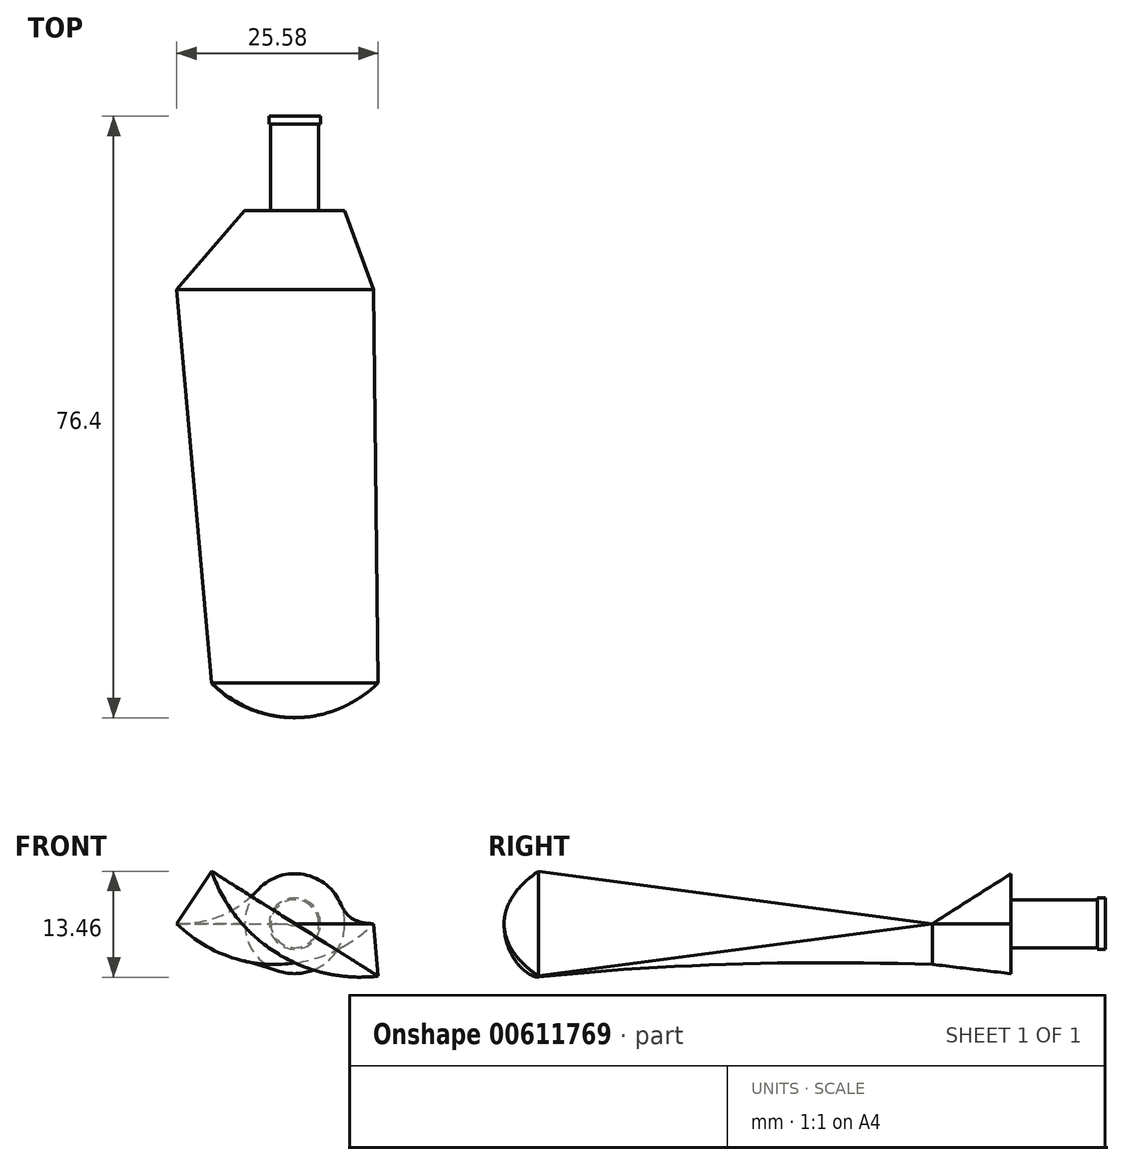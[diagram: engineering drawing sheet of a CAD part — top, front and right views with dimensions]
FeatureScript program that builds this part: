
annotation { "Feature Type Name" : "Feature", "Feature Type Description" : "" }
export const myFeature = defineFeature(function(context is Context, id is Id, definition is map)
    precondition{}
    {
        {
            var Q0;
            Q0=qCreatedBy(makeId("Front.planeOp"),FACE);
            var sketch = newSketch(context, id + "F0", { "sketchPlane" : qUnion([Q0])});
            skCircle(sketch, "E0", {"center": v(0, 0) * mm, "radius": 6.35 * mm});
            skSolve(sketch);
        }
        {
            var Q0;
            Q0=qCreatedBy(makeId("Front.planeOp"),FACE);
            cPlane(context, id + "F1", {"entities" : qUnion([Q0]), "cplaneType" : CPlaneType.OFFSET, "offset" : 10 * mm, "width" : 152.4 * mm, "height" : 152.4 * mm});
        }
        {
            var Q0;
            Q0=qCreatedBy(id+"F1.planeOp",FACE);
            cPlane(context, id + "F2", {"entities" : qUnion([Q0]), "cplaneType" : CPlaneType.OFFSET, "offset" : 50 * mm, "width" : 152.4 * mm, "height" : 152.4 * mm});
        }
        {
            var Q0;
            Q0=qCreatedBy(id+"F1.planeOp",FACE);
            var sketch = newSketch(context, id + "F3", { "sketchPlane" : qUnion([Q0])});
            skLineSegment(sketch, "E1", {"start": v(0, 0) * mm, "end": v(10, 0) * mm, "construction": true});
            skLineSegment(sketch, "E2", {"start": v(0, 0) * mm, "end": v(-15, 0) * mm, "construction": true});
            skLineSegment(sketch, "E3", {"start": v(0, 0) * mm, "end": v(0, 12.7) * mm, "construction": true});
            skLineSegment(sketch, "E4", {"start": v(0, 0) * mm, "end": v(0, -5) * mm, "construction": true});
            skArc(sketch, "E5", {"start": v(-15, 0) * mm, "mid": v(-2.5, -5.18) * mm, "end": v(10, 0) * mm});
            skLineSegment(sketch, "E6", {"start": v(-15, 0) * mm, "end": v(10, 0) * mm});
            skSolve(sketch);
        }
        {
            var Q0;
            Q0=qCreatedBy(id+"F2.planeOp",FACE);
            var sketch = newSketch(context, id + "F4", { "sketchPlane" : qUnion([Q0])});
            skLineSegment(sketch, "E7", {"start": v(0, 0) * mm, "end": v(12.7, 0) * mm, "construction": true});
            skLineSegment(sketch, "E8", {"start": v(0, 0) * mm, "end": v(-12.7, 0) * mm, "construction": true});
            skLineSegment(sketch, "E9", {"start": v(-12.7, 0) * mm, "end": v(-12.7, 8) * mm, "construction": true});
            skLineSegment(sketch, "E10", {"start": v(12.7, 0) * mm, "end": v(12.7, -8) * mm, "construction": true});
            skLineSegment(sketch, "E11", {"start": v(-12.7, 8) * mm, "end": v(12.7, -8) * mm, "construction": true});
            skLineSegment(sketch, "E12", {"start": v(0, 0) * mm, "end": v(-10.58, 6.66) * mm, "construction": true});
            skLineSegment(sketch, "E13", {"start": v(0, 0) * mm, "end": v(10.58, -6.66) * mm, "construction": true});
            skLineSegment(sketch, "E14", {"start": v(-10.58, 6.66) * mm, "end": v(10.58, -6.66) * mm});
            skArc(sketch, "E15", {"start": v(-10.58, 6.66) * mm, "mid": v(-2.34, -3.71) * mm, "end": v(10.58, -6.66) * mm});
            skSolve(sketch);
        }
        {
            var Q0;
            Q0=makeQuery(id+"F0.imprint","IMPRINT",FACE,{"disambiguationData":[TD([[makeQuery(id+"F0.imprint","IMPRINT",EDGE,{"derivedFrom":sQuery(id+"F0.wireOp",EDGE,"E0")}),1.0]])]});
            var Q1;
            Q1=makeQuery(id+"F3.imprint","IMPRINT",FACE,{"disambiguationData":[TD([[makeQuery(id+"F3.imprint","IMPRINT",EDGE,{"derivedFrom":sQuery(id+"F3.wireOp",EDGE,"E5")}),1.0]])]});
            loft(context, id + "F5", {"sheetProfilesArray" : [{ "sheetProfileEntities" : qUnion([Q0]) }, { "sheetProfileEntities" : qUnion([Q1]) }]});
        }
        {
            var Q1;
            Q1=makeQuery(id+"F3.imprint","IMPRINT",FACE,{"disambiguationData":[TD([[makeQuery(id+"F3.imprint","IMPRINT",EDGE,{"derivedFrom":sQuery(id+"F3.wireOp",EDGE,"E5")}),1.0]])]});
            var Q2;
            {var subQ0=sQuery(id+"F4.wireOp",EDGE,"E15");Q2=makeQuery(id+"F4.imprint","IMPRINT",FACE,{"disambiguationData":[TD([[makeQuery(id+"F4.imprint","IMPRINT",EDGE,{"derivedFrom":subQ0}),1.0]])]});}
            loft(context, id + "F6", {"operationType" : NewBodyOperationType.ADD, "sheetProfilesArray" : [{ "sheetProfileEntities" : qUnion([Q1]) }, { "sheetProfileEntities" : qUnion([Q2]) }]});
        }
        {
            var Q0;
            Q0=makeQuery(id+"F5.opLoft","CAP_FACE",FACE,{"disambiguationData":[OSD([makeQuery(id+"F0.imprint","IMPRINT",FACE,{"disambiguationData":[TD([[makeQuery(id+"F0.imprint","IMPRINT",EDGE,{"derivedFrom":sQuery(id+"F0.wireOp",EDGE,"E0")}),1.0]])]})])],"isStart":true});
            var sketch = newSketch(context, id + "F7", { "sketchPlane" : qUnion([Q0])});
            skCircle(sketch, "E16", {"center": v(0, 0) * mm, "radius": 3.05 * mm});
            skSolve(sketch);
        }
        {
            var Q0;
            Q0=qSketchRegion(id+"F7",true);
            extrude(context, id + "F8", {"entities" : qUnion([Q0]), "operationType" : NewBodyOperationType.ADD, "depth" : 11 * mm});
        }
        {
            var Q0;
            Q0=makeQuery(id+"F6.opLoft","CAP_FACE",FACE,{"disambiguationData":[OSD([makeQuery(id+"F4.imprint","IMPRINT",FACE,{"disambiguationData":[TD([[makeQuery(id+"F4.imprint","IMPRINT",EDGE,{"derivedFrom":sQuery(id+"F4.wireOp",EDGE,"E14")}),-1.0]])]})])],"isStart":true});
            var sketch = newSketch(context, id + "F9", { "sketchPlane" : qUnion([Q0])});
            skLineSegment(sketch, "E17.0.0", {"start": v(10.58, -6.66) * mm, "end": v(-10.58, 6.66) * mm});
            skFitSpline(sketch, "E17.0.1", {"points": [v(-10.58, 6.66) * mm, v(-10.4, 6.13) * mm, v(-10.19, 5.6) * mm, v(-9.96, 5.1) * mm, v(-9.73, 4.58) * mm, v(-9.48, 4.07) * mm, v(-9.2, 3.58) * mm, v(-8.94, 3.09) * mm, v(-8.65, 2.6) * mm, v(-8.33, 2.14) * mm, v(-8.02, 1.67) * mm, v(-7.7, 1.21) * mm, v(-7.34, 0.77) * mm, v(-7, 0.33) * mm, v(-6.62, -0.1) * mm, v(-6.24, -0.5) * mm, v(-5.85, -0.91) * mm, v(-5.45, -1.3) * mm, v(-5.03, -1.68) * mm, v(-4.61, -2.06) * mm, v(-4.18, -2.41) * mm, v(-3.73, -2.75) * mm, v(-3.28, -3.1) * mm, v(-2.82, -3.41) * mm, v(-2.34, -3.71) * mm, v(-1.86, -4.01) * mm, v(-1.37, -4.3) * mm, v(-0.87, -4.55) * mm, v(-0.37, -4.8) * mm, v(0.14, -5.05) * mm, v(0.66, -5.26) * mm, v(1.18, -5.48) * mm, v(1.7, -5.67) * mm, v(2.24, -5.84) * mm, v(2.78, -6.01) * mm, v(3.32, -6.16) * mm, v(3.87, -6.29) * mm, v(4.42, -6.41) * mm, v(4.97, -6.52) * mm, v(5.53, -6.6) * mm, v(6.08, -6.67) * mm, v(6.64, -6.73) * mm, v(7.2, -6.76) * mm, v(7.77, -6.8) * mm, v(8.33, -6.8) * mm, v(8.9, -6.78) * mm, v(9.46, -6.77) * mm, v(10.02, -6.73) * mm, v(10.58, -6.66) * mm]});
            skArc(sketch, "E18", {"start": v(-10.58, 6.66) * mm, "mid": v(-2.34, -3.71) * mm, "end": v(10.58, -6.66) * mm});
            skPoint(sketch, "E19", {"position": v(-2.34, -3.71) * mm});
            skSolve(sketch);
        }
        {
            var Q0;
            Q0=qSketchRegion(id+"F9",true);
            var Q1;
            Q1=sQuery(id+"F9.wireOp",EDGE,"E17.0.0");
            revolve(context, id + "F10", {"entities" : qUnion([Q0]), "axis" : qUnion([Q1]), "revolveType" : RevolveType.ONE_DIRECTION, "angle" : 90 * degree});
        }
        {
            var Q0;
            Q0=qSketchRegion(id+"F7",true);
            extrude(context, id + "F11", {"entities" : qUnion([Q0]), "operationType" : NewBodyOperationType.ADD, "depth" : 8 * mm});
        }
        {
            var Q0;
            Q0=makeQuery(id+"F8.opExtrude","CAP_FACE",FACE,{"disambiguationData":[OSD([sQuery(id+"F7.wireOp",EDGE,"E16")])],"isStart":false});
            var sketch = newSketch(context, id + "F12", { "sketchPlane" : qUnion([Q0])});
            skCircle(sketch, "E20", {"center": v(0, 0) * mm, "radius": 3.25 * mm});
            skSolve(sketch);
        }
        {
            var Q0;
            Q0=qSketchRegion(id+"F12",true);
            extrude(context, id + "F13", {"entities" : qUnion([Q0]), "operationType" : NewBodyOperationType.ADD, "depth" : 1 * mm});
        }
    });
